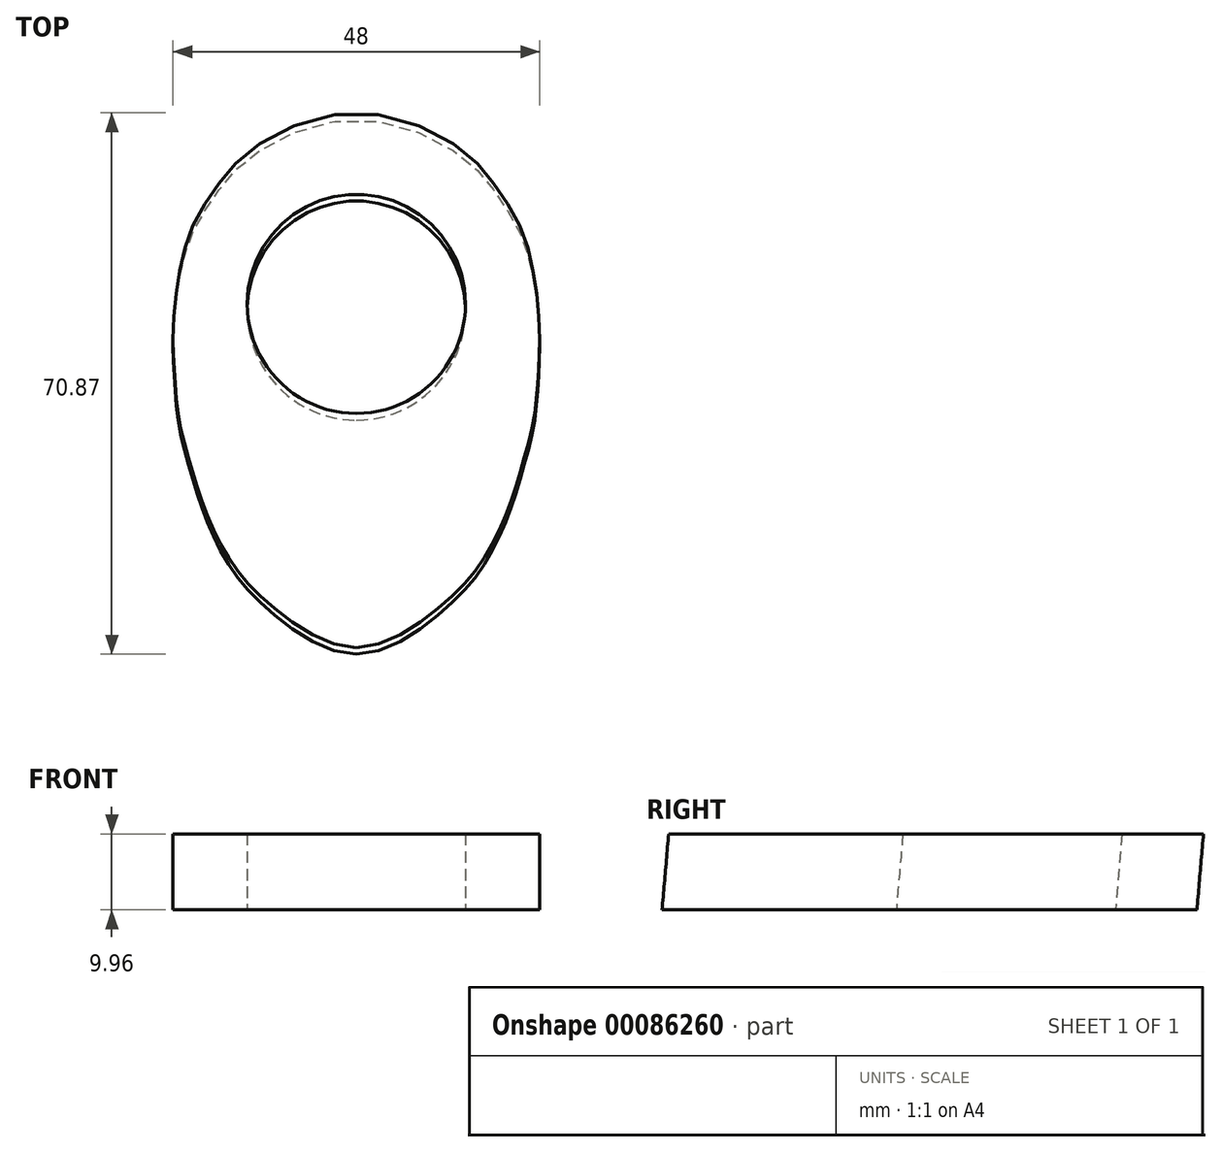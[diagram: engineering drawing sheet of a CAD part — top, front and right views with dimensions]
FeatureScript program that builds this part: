
annotation { "Feature Type Name" : "Feature", "Feature Type Description" : "" }
export const myFeature = defineFeature(function(context is Context, id is Id, definition is map)
    precondition{}
    {
        {
            var Q0;
            Q0=qCreatedBy(makeId("Top.planeOp"),FACE);
            var sketch = newSketch(context, id + "F0", { "sketchPlane" : qUnion([Q0])});
            skLineSegment(sketch, "E0", {"start": v(0, 0) * mm, "end": v(0, 5) * mm, "construction": true});
            skLineSegment(sketch, "E1", {"start": v(0, 5) * mm, "end": v(0, 10) * mm, "construction": true});
            skLineSegment(sketch, "E2", {"start": v(0, 10) * mm, "end": v(0, 15) * mm, "construction": true});
            skLineSegment(sketch, "E3", {"start": v(0, 15) * mm, "end": v(0, 20) * mm, "construction": true});
            skLineSegment(sketch, "E4", {"start": v(0, 20) * mm, "end": v(0, 25) * mm, "construction": true});
            skLineSegment(sketch, "E5", {"start": v(0, 25) * mm, "end": v(0, 30) * mm, "construction": true});
            skLineSegment(sketch, "E6", {"start": v(0, 30) * mm, "end": v(0, 35) * mm, "construction": true});
            skLineSegment(sketch, "E7", {"start": v(0, 35) * mm, "end": v(0, 40) * mm, "construction": true});
            skLineSegment(sketch, "E8", {"start": v(0, 40) * mm, "end": v(0, 45) * mm, "construction": true});
            skLineSegment(sketch, "E9", {"start": v(0, 45) * mm, "end": v(0, 50) * mm, "construction": true});
            skLineSegment(sketch, "E10", {"start": v(0, 50) * mm, "end": v(0, 55) * mm, "construction": true});
            skLineSegment(sketch, "E11", {"start": v(0, 55) * mm, "end": v(0, 60) * mm, "construction": true});
            skLineSegment(sketch, "E12", {"start": v(0, 60) * mm, "end": v(0, 65) * mm, "construction": true});
            skLineSegment(sketch, "E13", {"start": v(0, 65) * mm, "end": v(0, 70) * mm, "construction": true});
            skLineSegment(sketch, "E14", {"start": v(0, 10) * mm, "end": v(-15.5, 10) * mm, "construction": true});
            skLineSegment(sketch, "E15", {"start": v(0, 15) * mm, "end": v(-18.5, 15) * mm, "construction": true});
            skLineSegment(sketch, "E16", {"start": v(0, 20) * mm, "end": v(-20.5, 20) * mm, "construction": true});
            skLineSegment(sketch, "E17", {"start": v(0, 25) * mm, "end": v(-22, 25) * mm, "construction": true});
            skLineSegment(sketch, "E18", {"start": v(0, 30) * mm, "end": v(-23.25, 30) * mm, "construction": true});
            skLineSegment(sketch, "E19", {"start": v(0, 35) * mm, "end": v(-23.75, 35) * mm, "construction": true});
            skLineSegment(sketch, "E20", {"start": v(0, 40) * mm, "end": v(-24, 40) * mm, "construction": true});
            skLineSegment(sketch, "E21", {"start": v(0, 45) * mm, "end": v(-23.75, 45) * mm, "construction": true});
            skLineSegment(sketch, "E22", {"start": v(0, 50) * mm, "end": v(-23, 50) * mm, "construction": true});
            skLineSegment(sketch, "E23", {"start": v(0, 55) * mm, "end": v(-21.5, 55) * mm, "construction": true});
            skLineSegment(sketch, "E24", {"start": v(0, 65) * mm, "end": v(-14, 65) * mm, "construction": true});
            skLineSegment(sketch, "E25", {"start": v(0, 60) * mm, "end": v(-18.5, 60) * mm, "construction": true});
            skLineSegment(sketch, "E26", {"start": v(0, 10) * mm, "end": v(15.5, 10) * mm, "construction": true});
            skLineSegment(sketch, "E27", {"start": v(0, 15) * mm, "end": v(18.5, 15) * mm, "construction": true});
            skLineSegment(sketch, "E28", {"start": v(0, 20) * mm, "end": v(20.5, 20) * mm, "construction": true});
            skLineSegment(sketch, "E29", {"start": v(0, 25) * mm, "end": v(22, 25) * mm, "construction": true});
            skLineSegment(sketch, "E30", {"start": v(0, 30) * mm, "end": v(23.25, 30) * mm, "construction": true});
            skLineSegment(sketch, "E31", {"start": v(0, 35) * mm, "end": v(23.75, 35) * mm, "construction": true});
            skLineSegment(sketch, "E32", {"start": v(0, 40) * mm, "end": v(24, 40) * mm, "construction": true});
            skLineSegment(sketch, "E33", {"start": v(0, 45) * mm, "end": v(23.75, 45) * mm, "construction": true});
            skLineSegment(sketch, "E34", {"start": v(0, 50) * mm, "end": v(23, 50) * mm, "construction": true});
            skLineSegment(sketch, "E35", {"start": v(0, 55) * mm, "end": v(21.5, 55) * mm, "construction": true});
            skLineSegment(sketch, "E36", {"start": v(0, 60) * mm, "end": v(18.5, 60) * mm, "construction": true});
            skLineSegment(sketch, "E37", {"start": v(0, 65) * mm, "end": v(14, 65) * mm, "construction": true});
            skLineSegment(sketch, "E38", {"start": v(0, 5) * mm, "end": v(-10.5, 5) * mm, "construction": true});
            skLineSegment(sketch, "E39", {"start": v(0, 5) * mm, "end": v(10.5, 5) * mm, "construction": true});
            skFitSpline(sketch, "E40", {"points": [v(0, 0) * mm, v(-10.5, 5) * mm, v(-15.5, 10) * mm, v(-18.5, 15) * mm, v(-20.5, 20) * mm, v(-22, 25) * mm, v(-23.25, 30) * mm, v(-23.75, 35) * mm, v(-24, 40) * mm, v(-23.75, 45) * mm, v(-23, 50) * mm, v(-21.5, 55) * mm, v(-18.5, 60) * mm, v(-14, 65) * mm, v(0, 70) * mm, v(14, 65) * mm, v(18.5, 60) * mm, v(21.5, 55) * mm, v(23, 50) * mm, v(23.75, 45) * mm, v(24, 40) * mm, v(23.75, 35) * mm, v(23.25, 30) * mm, v(22, 25) * mm, v(20.5, 20) * mm, v(18.5, 15) * mm, v(15.5, 10) * mm, v(10.5, 5) * mm, v(0, 0) * mm]});
            skSolve(sketch);
        }
        {
            var Q0;
            Q0=sQuery(id+"F0.wireOp",EDGE,"E21");
            cPlane(context, id + "F1", {"entities" : qUnion([Q0]), "cplaneType" : CPlaneType.LINE_ANGLE, "offset" : 150 * mm, "angle" : 95 * degree, "width" : 150 * mm, "height" : 150 * mm});
        }
        {
            var Q0;
            Q0=qCreatedBy(id+"F1.planeOp",FACE);
            var sketch = newSketch(context, id + "F2", { "sketchPlane" : qUnion([Q0])});
            skCircle(sketch, "E41", {"center": v(0, 44.83) * mm, "radius": 14.29 * mm});
            skSolve(sketch);
        }
        {
            var Q0;
            Q0=qCreatedBy(makeId("Right.planeOp"),FACE);
            var sketch = newSketch(context, id + "F3", { "sketchPlane" : qUnion([Q0])});
            skLineSegment(sketch, "E42", {"start": v(45, 0) * mm, "end": v(45.87, 9.96) * mm});
            skLineSegment(sketch, "E43", {"start": v(45, 0) * mm, "end": v(45, 25.9) * mm, "construction": true});
            skSolve(sketch);
        }
        {
            var Q0;
            Q0=makeQuery(id+"F0.imprint","IMPRINT",FACE,{"disambiguationData":[TD([[makeQuery(id+"F0.imprint","IMPRINT",EDGE,{"derivedFrom":sQuery(id+"F0.wireOp",EDGE,"E40")}),-1.0]])]});
            var Q1;
            Q1=sQuery(id+"F3.wireOp",EDGE,"E42");
            sweep(context, id + "F4", {"profiles" : qUnion([Q0]), "path" : qUnion([Q1])});
        }
        {
            var Q0;
            Q0 = qSketchRegion(id + "F2", true);
            extrude(context, id + "F5", {"entities" : qUnion([Q0]), "operationType" : NewBodyOperationType.REMOVE, "endBound" : BoundingType.SYMMETRIC, "depth" : 25 * mm});
        }
    });
